# Revit family: IS_Cerasprint_B5347_BIM_GB
name_source: partatom
category: Plumbing Fixtures
revit_build: Autodesk Revit MEP 2014 (Build: 20130308_1515(x64)
units: mm (PartAtom-declared; Revit-internal decimal feet)

## types (1)
- B5347AA - Cerasprint Sink Mixer 1 Hole Ceramic Disc Single Lever, Pull Out 2 Function Swivel Spout
    Accessories = www.idealspec.co.uk
    AreaUnits = millimeters
    Assembly Code = C1030200
    AssetType = Fixed
    BIMObjectName = ISI_IdealStandard_MixerTaps_Cerasprint_B5347AA
    BREEAMApproved = No
    BarCode = 3800019252721
    Brand = Ideal Standard
    CWFU = 0
    Color = Chrome
    ConnectionType = Plumbing
    Cost = 0 $
    Default Elevation = 0 mm  [stored 0 ft]
    Description = Cerasprint sink mixer 1 hole ceramic disc single lever, pull out 2 function swivel spout
    DurationUnit = year
    ECA = No
    ExpectedLife = 30
    FaucetFunction = MIXED
    FaucetOperation = LEVERHANDLE
    FaucetType = OTHER
    Features = Sink mixer 1 hole ceramic disc single lever, pull out 2 function swivel spout
    Finish = Chrome
    FlowRate = 6L/min @ 3Bar
    HWFU = 0
    Help = www.idealspec.co.uk/contact-us.html
    IfcExportAs = IfcValveType
    IfcExportType = FAUCET
    InstallationInstructions = www.idealspec.co.uk/resources.html
    LinearUnits = millimeters
    ManufacturerURL = www.idealspec.co.uk
    Material = Brass
    Model = B5347AA
    ModelNumber = B5347AA
    ModelReference = Cerasprint sink mixer 1 hole ceramic disc single lever, pull out 2 function swivel spout
    NBSDescription = Water supply fittings for sinks
    NBSReference = 45-35-70/345
    Name = MixerTaps_Cerasprint_B5347AA_IdealStandard
    NettWeight = 2.98 Kg
    NominalHeight = 199 mm
    NominalLength = 277 mm
    NominalWidth = 58 mm
    ProductInformation = www.idealspec.co.uk/assets/datasheet/B5347AA
    Shape = Sculptured
    Size = 199 x 278 x 59 mm
    Space = Internal
    SpareParts = www.fastpart-spares.co.uk
    TMV3 = No
    TestPressure = 10 Bar
    URL = www.idealspec.co.uk
    Version = 2
    VolumeUnits = Litres
    WFU = 0
    WRAS = No
    WarrantyDescription = Manufacturers Warranty
    WarrantyDurationParts = 5
    WarrantyDurationUnit = year
    WaterEfficientProduct = No
    WorkingPressure = 3 Bar

note: [stored X ft] marks values corroborated as IEEE doubles in the binary element streams (Revit-internal decimal feet)

## geometry (parser evidence)
native form markers: Sweep x3
no freeform markers — native parametric forms only
